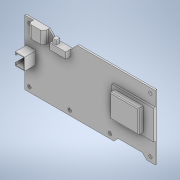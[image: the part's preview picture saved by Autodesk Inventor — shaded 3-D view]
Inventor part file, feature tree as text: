
AUTODESK INVENTOR PART (.ipt)
format: ipt  version: 2021 (Build 250183000, 183)  size: 297,984 bytes
history: native  units: mm
features: sketch x14, extrude x12, fillet x3, chamfer x2, hole x2
ambient origin geometry x8: Origin, YZ Plane, XZ Plane, XY Plane, X Axis, Y Axis, Z Axis, Center Point
bodies: Solid1 (feature_tree)
feature tree (33):
  extrude  "Extrusion1"  Depth=40.0mm
  extrude  "Extrusion2"  Depth=1.0mm
  chamfer  "Chamfer1"  Distance=1.0mm
  extrude  "Extrusion3"  Depth=28.8mm
  fillet  "Fillet1"  Radius=3.9mm
  extrude  "Extrusion4"  Depth=2.0mm TaperAngle=45.0deg
  extrude  "Extrusion5"  Depth=14.73mm
  hole  "Hole1"  [1 undecoded]
  hole  "Hole2"  [1 undecoded]
  extrude  "Extrusion6"  Depth=3.2mm TaperAngle=0.0deg
  chamfer  "Chamfer2"  Distance=2.8mm
  extrude  "Extrusion7"  Depth=3.0mm
  extrude  "Extrusion8"  Depth=2.2mm
  extrude  "Extrusion9"  Depth=3.0mm
  extrude  "Extrusion10"  Depth=3.0mm
  fillet  "Fillet2"  Radius=3.0mm
  extrude  "Extrusion11"  Depth=3.0mm
  fillet  "Fillet3"  Radius=3.0mm
  extrude  "Extrusion12"  Depth=37.0mm
  sketch  "Sketch1"  dims[d0=81.0mm d1=40.0mm]
  sketch  "Sketch2"  dims[d2=20.0mm d3=40.5mm d4=1.0mm d5=0.0mm]
  sketch  "Sketch3"  dims[d6=18.7mm d7=28.8mm d8=3.9mm]
  sketch  "Sketch4"  dims[d9=1.0mm d10=0.0mm d11=3.88mm d12=2.0mm d13=45.0deg]
  sketch  "Sketch5"  dims[d14=5.46mm d15=14.73mm]
  sketch  "Sketch6"  dims[d16=7.62mm d17=3.2mm d18=0.0mm]
  sketch  "Sketch7"  dims[d19=2.0mm d20=3.8mm]
  sketch  "Sketch8"  dims[d21=10.0mm d22=3.2mm d23=0.0mm]
  sketch  "Sketch9"  dims[d24=0.6mm]
  sketch  "Sketch10"  dims[d25=1.2mm]
  sketch  "Sketch11"  dims[d26=2.4mm]
  sketch  "Sketch12"  dims[d27=2.2mm d28=2.8mm d29=0.0mm]
  sketch  "Sketch13"  dims[d30=3.0mm d31=28.0mm]
  sketch  "Sketch14"  dims[d32=53.0mm d33=78.0mm d34=3.0mm d35=3.0mm d36=3.0mm d37=3.0mm d38=2.0mm d39=6.0mm d40=4.0mm d41=2.0mm d42=90.0deg d43=4.0mm d44=20.594885mm d45=3.0mm d46=37.0mm d47=78.0mm d48=37.0mm d49=2.0mm d50=6.0mm d51=4.0mm d52=2.0mm d53=90.0deg d54=4.0mm d55=20.594885mm d56=58.0mm d57=73.0mm d58=2.7mm d59=2.0mm d60=0.0mm d61=2.7mm d62=2.0mm d63=45.0deg d64=1.14mm d65=7.0mm d66=16.9mm d67=24.4mm d68=0.5mm d69=0.5mm d70=0.5mm d71=0.5mm d72=1.2mm d73=1.2mm d74=7.0mm d75=0.0mm d76=5.0mm d77=0.0mm d78=55.0mm d79=9.0mm d80=18.2mm d81=1.0mm d82=0.0mm d83=2.0mm d84=2.0mm d85=2.0mm d86=6.5mm d87=3.0mm d88=0.0mm d89=0.5mm d90=36.1mm d91=44.9mm d92=0.6mm d93=3.9mm d94=6.0mm d95=0.0mm d96=1.0mm d97=57.8mm d98=73.0mm d99=15.0mm d100=2.2mm d101=0.0mm]
note: 2 required parameter values undecoded (feature->parameter linkage not recoverable at this tier; creation-order binding heuristic only, values carry confidence <= 0.55)
